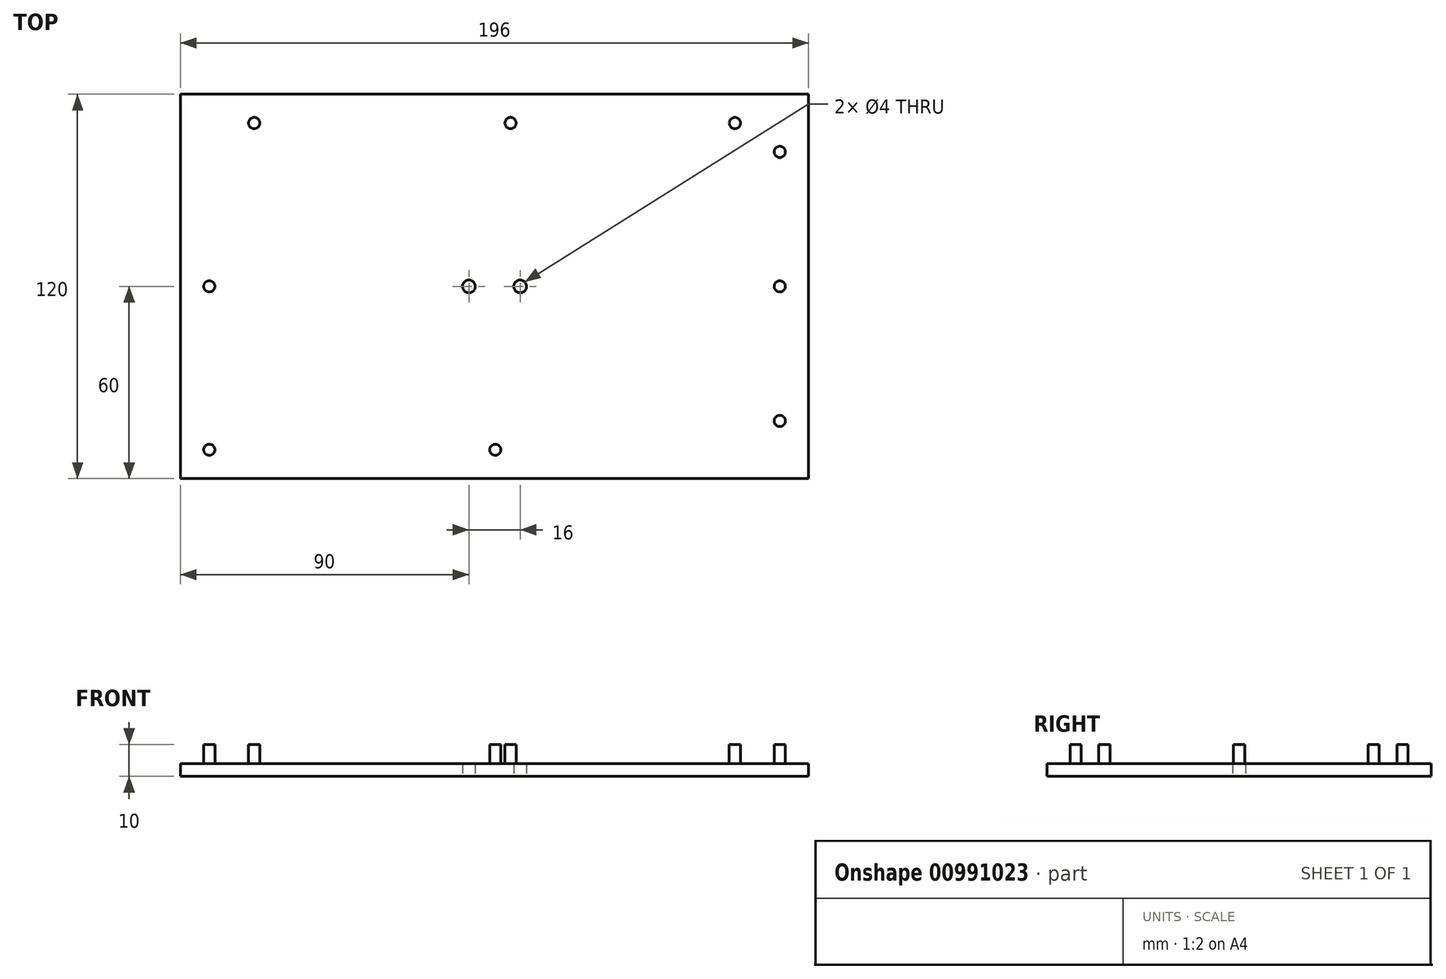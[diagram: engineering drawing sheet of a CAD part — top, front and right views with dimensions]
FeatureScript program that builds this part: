
annotation { "Feature Type Name" : "Feature", "Feature Type Description" : "" }
export const myFeature = defineFeature(function(context is Context, id is Id, definition is map)
    precondition{}
    {
        {
            var Q0;
            Q0=qCreatedBy(makeId("Top.planeOp"),FACE);
            var sketch = newSketch(context, id + "F0", { "sketchPlane" : qUnion([Q0])});
            skLineSegment(sketch, "E0.bottom", {"start": v(-75.26, 60) * mm, "end": v(120.74, 60) * mm});
            skLineSegment(sketch, "E0.top", {"start": v(-75.26, -60) * mm, "end": v(120.74, -60) * mm});
            skLineSegment(sketch, "E0.left", {"start": v(-75.26, 60) * mm, "end": v(-75.26, -60) * mm});
            skLineSegment(sketch, "E0.right", {"start": v(120.74, 60) * mm, "end": v(120.74, -60) * mm});
            skLineSegment(sketch, "E1", {"start": v(120.74, 0) * mm, "end": v(-75.26, 0) * mm, "construction": true});
            skLineSegment(sketch, "E2", {"start": v(22.74, 60) * mm, "end": v(22.74, -60) * mm, "construction": true});
            skPoint(sketch, "E2.endSnap0", {"position": v(22.74, -60) * mm});
            skCircle(sketch, "E3", {"center": v(30.74, 0) * mm, "radius": 2 * mm});
            skCircle(sketch, "E4.MirrorC", {"center": v(14.74, 0) * mm, "radius": 2 * mm});
            skSolve(sketch);
        }
        {
            var Q0;
            Q0 = qSketchRegion(id + "F0", true);
            extrude(context, id + "F1", {"entities" : qUnion([Q0]), "depth" : 4 * mm, "offsetDistance" : 25 * mm});
        }
        {
            var Q0;
            Q0=makeQuery(id+"F1.opExtrude","CAP_FACE",FACE,{"disambiguationData":[OSD([sQuery(id+"F0.wireOp",EDGE,"E0.bottom"),sQuery(id+"F0.wireOp",EDGE,"E0.top"),sQuery(id+"F0.wireOp",EDGE,"E0.left"),sQuery(id+"F0.wireOp",EDGE,"E0.right")])],"isStart":false});
            var sketch = newSketch(context, id + "F2", { "sketchPlane" : qUnion([Q0])});
            skCircle(sketch, "E5", {"center": v(-66.26, -51) * mm, "radius": 1.75 * mm});
            skCircle(sketch, "E6", {"center": v(22.99, -51) * mm, "radius": 1.75 * mm});
            skCircle(sketch, "E7", {"center": v(111.74, -42) * mm, "radius": 1.75 * mm});
            skCircle(sketch, "E8", {"center": v(111.74, 42) * mm, "radius": 1.75 * mm});
            skCircle(sketch, "E9", {"center": v(-52.26, 51) * mm, "radius": 1.75 * mm});
            skCircle(sketch, "E10", {"center": v(-66.26, 0) * mm, "radius": 1.75 * mm});
            skCircle(sketch, "E11", {"center": v(97.74, 51) * mm, "radius": 1.75 * mm});
            skCircle(sketch, "E12", {"center": v(27.74, 51) * mm, "radius": 1.75 * mm});
            skCircle(sketch, "E13", {"center": v(111.74, 0) * mm, "radius": 1.75 * mm});
            skCircle(sketch, "E14", {"center": v(30.86, 0) * mm, "radius": 2 * mm});
            skLineSegment(sketch, "E15", {"start": v(22.74, -60) * mm, "end": v(22.99, 60) * mm, "construction": true});
            skPoint(sketch, "E15.endSnap0", {"position": v(22.74, 60) * mm});
            skLineSegment(sketch, "E16", {"start": v(120.74, 0) * mm, "end": v(-75.26, 0) * mm, "construction": true});
            skCircle(sketch, "E17.MirrorC", {"center": v(14.86, 0.03) * mm, "radius": 2 * mm});
            skSolve(sketch);
        }
        {
            var Q0;
            Q0=makeQuery(id+"F2.imprint","IMPRINT",FACE,{"disambiguationData":[TD([[makeQuery(id+"F2.imprint","IMPRINT",EDGE,{"derivedFrom":sQuery(id+"F2.wireOp",EDGE,"E5")}),1.0]])]});
            var Q1;
            Q1=makeQuery(id+"F2.imprint","IMPRINT",FACE,{"disambiguationData":[TD([[makeQuery(id+"F2.imprint","IMPRINT",EDGE,{"derivedFrom":sQuery(id+"F2.wireOp",EDGE,"E6")}),1.0]])]});
            var Q2;
            Q2=makeQuery(id+"F2.imprint","IMPRINT",FACE,{"disambiguationData":[TD([[makeQuery(id+"F2.imprint","IMPRINT",EDGE,{"derivedFrom":sQuery(id+"F2.wireOp",EDGE,"E7")}),1.0]])]});
            var Q3;
            Q3=makeQuery(id+"F2.imprint","IMPRINT",FACE,{"disambiguationData":[TD([[makeQuery(id+"F2.imprint","IMPRINT",EDGE,{"derivedFrom":sQuery(id+"F2.wireOp",EDGE,"E8")}),1.0]])]});
            var Q4;
            Q4=makeQuery(id+"F2.imprint","IMPRINT",FACE,{"disambiguationData":[TD([[makeQuery(id+"F2.imprint","IMPRINT",EDGE,{"derivedFrom":sQuery(id+"F2.wireOp",EDGE,"E9")}),1.0]])]});
            var Q5;
            Q5=makeQuery(id+"F2.imprint","IMPRINT",FACE,{"disambiguationData":[TD([[makeQuery(id+"F2.imprint","IMPRINT",EDGE,{"derivedFrom":sQuery(id+"F2.wireOp",EDGE,"E10")}),1.0]])]});
            var Q6;
            Q6=makeQuery(id+"F2.imprint","IMPRINT",FACE,{"disambiguationData":[TD([[makeQuery(id+"F2.imprint","IMPRINT",EDGE,{"derivedFrom":sQuery(id+"F2.wireOp",EDGE,"E11")}),1.0]])]});
            var Q7;
            Q7=makeQuery(id+"F2.imprint","IMPRINT",FACE,{"disambiguationData":[TD([[makeQuery(id+"F2.imprint","IMPRINT",EDGE,{"derivedFrom":sQuery(id+"F2.wireOp",EDGE,"E12")}),1.0]])]});
            var Q8;
            Q8=makeQuery(id+"F2.imprint","IMPRINT",FACE,{"disambiguationData":[TD([[makeQuery(id+"F2.imprint","IMPRINT",EDGE,{"derivedFrom":sQuery(id+"F2.wireOp",EDGE,"E13")}),1.0]])]});
            extrude(context, id + "F3", {"entities" : qUnion([Q0, Q1, Q2, Q3, Q4, Q5, Q6, Q7, Q8]), "operationType" : NewBodyOperationType.ADD, "depth" : 6 * mm, "offsetDistance" : 25 * mm});
        }
    });
